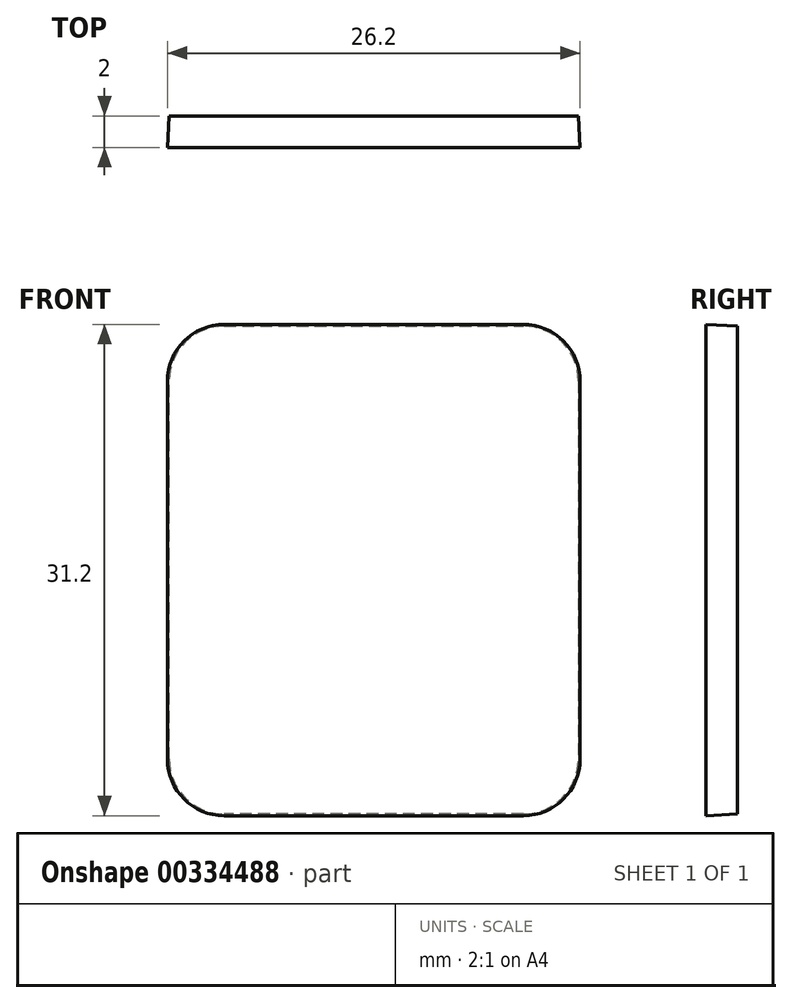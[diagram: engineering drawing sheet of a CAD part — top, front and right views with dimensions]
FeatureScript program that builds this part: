
annotation { "Feature Type Name" : "Feature", "Feature Type Description" : "" }
export const myFeature = defineFeature(function(context is Context, id is Id, definition is map)
    precondition{}
    {
        {
            var Q0;
            Q0=qCreatedBy(makeId("Front.planeOp"),FACE);
            var sketch = newSketch(context, id + "F0", { "sketchPlane" : qUnion([Q0])});
            skLineSegment(sketch, "E0.bottom", {"start": v(9.5, 15.5) * mm, "end": v(-9.5, 15.5) * mm});
            skLineSegment(sketch, "E0.top", {"start": v(9.5, -15.5) * mm, "end": v(-9.5, -15.5) * mm});
            skLineSegment(sketch, "E0.left", {"start": v(13, 12) * mm, "end": v(13, -12) * mm});
            skLineSegment(sketch, "E0.right", {"start": v(-13, 12) * mm, "end": v(-13, -12) * mm});
            skPoint(sketch, "E0.middle", {"position": v(0, 0) * mm});
            skPoint(sketch, "E1.visualSharp", {"position": v(-13, 15.5) * mm});
            skArc(sketch, "E1.filletArc", {"start": v(-9.5, 15.5) * mm, "mid": v(-11.97, 14.47) * mm, "end": v(-13, 12) * mm});
            skPoint(sketch, "E2.visualSharp", {"position": v(13, 15.5) * mm});
            skArc(sketch, "E2.filletArc", {"start": v(13, 12) * mm, "mid": v(11.97, 14.47) * mm, "end": v(9.5, 15.5) * mm});
            skPoint(sketch, "E3.visualSharp", {"position": v(-13, -15.5) * mm});
            skArc(sketch, "E3.filletArc", {"start": v(-13, -12) * mm, "mid": v(-11.97, -14.47) * mm, "end": v(-9.5, -15.5) * mm});
            skPoint(sketch, "E4.visualSharp", {"position": v(13, -15.5) * mm});
            skArc(sketch, "E4.filletArc", {"start": v(9.5, -15.5) * mm, "mid": v(11.97, -14.47) * mm, "end": v(13, -12) * mm});
            skSolve(sketch);
        }
        {
            var Q0;
            Q0=makeQuery(id+"F0.imprint","IMPRINT",FACE,{"disambiguationData":[TD([[makeQuery(id+"F0.imprint","IMPRINT",EDGE,{"derivedFrom":sQuery(id+"F0.wireOp",EDGE,"E0.bottom")}),1.0]])]});
            extrude(context, id + "F1", {"entities" : qUnion([Q0]), "depth" : 2 * mm, "hasDraft" : true, "draftAngle" : 3 * degree});
        }
    });
